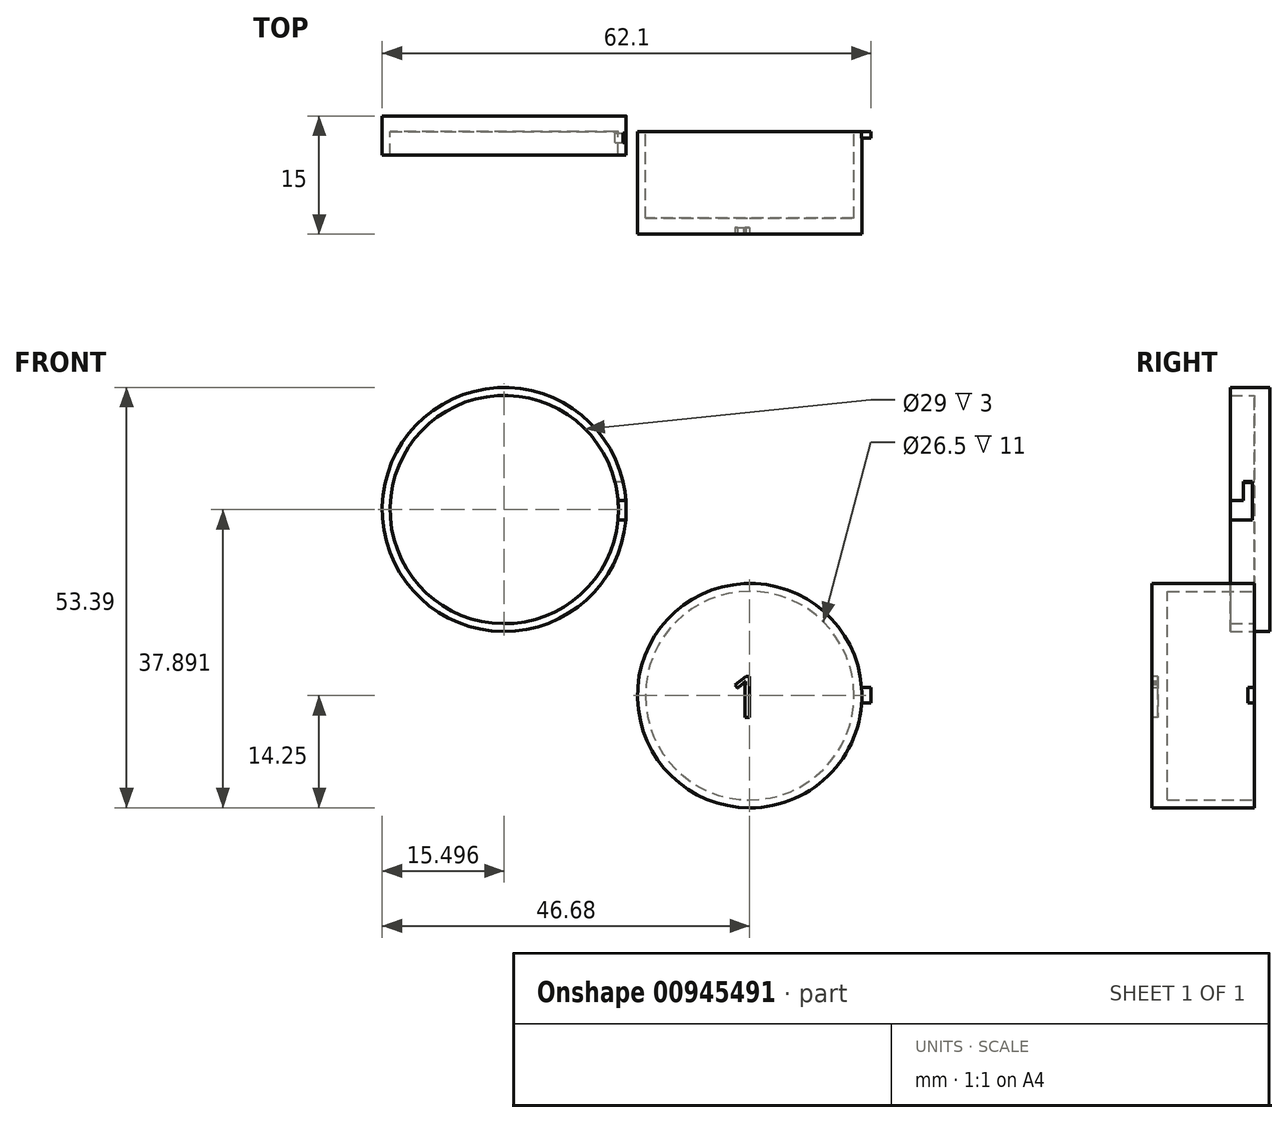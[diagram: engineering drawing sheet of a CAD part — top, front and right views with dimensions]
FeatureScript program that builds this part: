
annotation { "Feature Type Name" : "Feature", "Feature Type Description" : "" }
export const myFeature = defineFeature(function(context is Context, id is Id, definition is map)
    precondition{}
    {
        {
            var Q0;
            Q0=qCreatedBy(makeId("Front.planeOp"),FACE);
            var sketch = newSketch(context, id + "F0", { "sketchPlane" : qUnion([Q0])});
            skCircle(sketch, "E0", {"center": v(0, 0) * mm, "radius": 13.25 * mm});
            skCircle(sketch, "E1", {"center": v(0, 0) * mm, "radius": 14.25 * mm});
            skSolve(sketch);
        }
        {
            var Q0;
            Q0=makeQuery(id+"F0.imprint","IMPRINT",FACE,{"disambiguationData":[TD([[makeQuery(id+"F0.imprint","IMPRINT",EDGE,{"derivedFrom":sQuery(id+"F0.wireOp",EDGE,"E0")}),-1.0]])]});
            extrude(context, id + "F1", {"entities" : qUnion([Q0]), "depth" : 11 * mm, "offsetDistance" : 25 * mm});
        }
        {
            var Q0;
            Q0=makeQuery(id+"F1.opExtrude","CAP_FACE",FACE,{"disambiguationData":[OSD([sQuery(id+"F0.wireOp",EDGE,"E0"),sQuery(id+"F0.wireOp",EDGE,"E1")])],"isStart":false});
            var sketch = newSketch(context, id + "F2", { "sketchPlane" : qUnion([Q0])});
            skCircle(sketch, "E2", {"center": v(0, 0) * mm, "radius": 14.25 * mm});
            skSolve(sketch);
        }
        {
            var Q0;
            Q0 = qSketchRegion(id + "F2", true);
            extrude(context, id + "F3", {"entities" : qUnion([Q0]), "operationType" : NewBodyOperationType.ADD, "depth" : 2 * mm, "offsetDistance" : 25 * mm});
        }
        {
            var Q0;
            Q0=qCreatedBy(makeId("Front.planeOp"),FACE);
            var sketch = newSketch(context, id + "F4", { "sketchPlane" : qUnion([Q0])});
            skCircle(sketch, "E3", {"center": v(-31.18, 23.64) * mm, "radius": 14.5 * mm});
            skCircle(sketch, "E4", {"center": v(-31.18, 23.64) * mm, "radius": 15.5 * mm});
            skSolve(sketch);
        }
        {
            var Q0;
            Q0=makeQuery(id+"F4.imprint","IMPRINT",FACE,{"disambiguationData":[TD([[makeQuery(id+"F4.imprint","IMPRINT",EDGE,{"derivedFrom":sQuery(id+"F4.wireOp",EDGE,"E3")}),-1.0]])]});
            extrude(context, id + "F5", {"entities" : qUnion([Q0]), "depth" : 3 * mm, "offsetDistance" : 25 * mm});
        }
        {
            var Q0;
            Q0=makeQuery(id+"F5.opExtrude","CAP_FACE",FACE,{"disambiguationData":[OSD([sQuery(id+"F4.wireOp",EDGE,"E3"),sQuery(id+"F4.wireOp",EDGE,"E4")])],"isStart":true});
            var sketch = newSketch(context, id + "F6", { "sketchPlane" : qUnion([Q0])});
            skCircle(sketch, "E5", {"center": v(31.18, 23.64) * mm, "radius": 15.5 * mm});
            skSolve(sketch);
        }
        {
            var Q0;
            Q0 = qSketchRegion(id + "F6", true);
            extrude(context, id + "F7", {"entities" : qUnion([Q0]), "operationType" : NewBodyOperationType.ADD, "depth" : 2 * mm, "offsetDistance" : 25 * mm});
        }
        {
            var Q0;
            Q0=makeQuery(id+"F1.opExtrude","CAP_FACE",FACE,{"disambiguationData":[OSD([sQuery(id+"F0.wireOp",EDGE,"E0"),sQuery(id+"F0.wireOp",EDGE,"E1")])],"isStart":true});
            var sketch = newSketch(context, id + "F8", { "sketchPlane" : qUnion([Q0])});
            skLineSegment(sketch, "E6.bottom", {"start": v(-14.22, -0.95) * mm, "end": v(-15.42, -0.95) * mm});
            skLineSegment(sketch, "E6.top", {"start": v(-14.22, 1.05) * mm, "end": v(-15.42, 1.05) * mm});
            skLineSegment(sketch, "E6.left", {"start": v(-14.22, -0.95) * mm, "end": v(-14.22, 1.05) * mm});
            skLineSegment(sketch, "E6.right", {"start": v(-15.42, -0.95) * mm, "end": v(-15.42, 1.05) * mm});
            skSolve(sketch);
        }
        {
            var Q0;
            {var subQ4=sQuery(id+"F8.wireOp",EDGE,"E6.bottom");Q0=makeQuery(id+"F8.imprint","IMPRINT",FACE,{"disambiguationData":[TD([[makeQuery(id+"F8.imprint","IMPRINT",EDGE,{"derivedFrom":subQ4}),-1.0]])]});}
            extrude(context, id + "F9", {"entities" : qUnion([Q0]), "operationType" : NewBodyOperationType.ADD, "oppositeDirection" : true, "depth" : 0.8 * mm, "offsetDistance" : 25 * mm});
        }
        {
            var Q0;
            Q0=makeQuery(id+"F5.opExtrude","CAP_FACE",FACE,{"disambiguationData":[OSD([sQuery(id+"F4.wireOp",EDGE,"E3"),sQuery(id+"F4.wireOp",EDGE,"E4")])],"isStart":false});
            var sketch = newSketch(context, id + "F10", { "sketchPlane" : qUnion([Q0])});
            skLineSegment(sketch, "E7.bottom", {"start": v(-17.06, 22.3) * mm, "end": v(-15.06, 22.3) * mm});
            skLineSegment(sketch, "E7.right", {"start": v(-15.06, 22.3) * mm, "end": v(-15.06, 24.8) * mm});
            skLineSegment(sketch, "E8", {"start": v(-15.06, 24.8) * mm, "end": v(-17.06, 24.8) * mm});
            skLineSegment(sketch, "E9", {"start": v(-17.06, 24.8) * mm, "end": v(-17.06, 22.3) * mm});
            skSolve(sketch);
        }
        {
            var Q0;
            Q0 = qSketchRegion(id + "F10", true);
            extrude(context, id + "F11", {"entities" : qUnion([Q0]), "operationType" : NewBodyOperationType.REMOVE, "oppositeDirection" : true, "depth" : 2.8 * mm, "offsetDistance" : 25 * mm});
        }
        {
            var Q0;
            Q0=makeQuery(id+"F11.boolean.opBoolean","COPY",FACE,{"derivedFrom":makeQuery(id+"F11.opExtrude","SWEPT_FACE",FACE,{"disambiguationData":[OSD([sQuery(id+"F10.wireOp",EDGE,"E8")])]})});
            var sketch = newSketch(context, id + "F12", { "sketchPlane" : qUnion([Q0])});
            skLineSegment(sketch, "E10.left", {"start": v(-17.1, 0.2) * mm, "end": v(-17.1, 1.4) * mm});
            skLineSegment(sketch, "E10.right", {"start": v(-15.18, 0.2) * mm, "end": v(-15.18, 1.4) * mm});
            skLineSegment(sketch, "E11", {"start": v(-17.1, 1.4) * mm, "end": v(-15.18, 1.4) * mm});
            skLineSegment(sketch, "E12", {"start": v(-17.1, 0.2) * mm, "end": v(-15.18, 0.2) * mm});
            skSolve(sketch);
        }
        {
            var Q0;
            Q0 = qSketchRegion(id + "F12", true);
            extrude(context, id + "F13", {"entities" : qUnion([Q0]), "operationType" : NewBodyOperationType.REMOVE, "oppositeDirection" : true, "depth" : 2.4 * mm, "offsetDistance" : 25 * mm});
        }
        {
            var Q0;
            Q0=makeQuery(id+"F3.opExtrude","CAP_FACE",FACE,{"disambiguationData":[OSD([sQuery(id+"F2.wireOp",EDGE,"E2")])],"isStart":false});
            var sketch = newSketch(context, id + "F14", { "sketchPlane" : qUnion([Q0])});
            skText(sketch, "E13", { "text": "1", "fontName": "OpenSans-Regular.ttf"});
            const initialGuessF14  = {"E13": [-0.00254, -0.00277, 1, 0, 0.00524]};
            skSetInitialGuess(sketch, initialGuessF14);
            skSolve(sketch);
        }
        {
            var Q0;
            Q0 = qSketchRegion(id + "F14", true);
            extrude(context, id + "F15", {"entities" : qUnion([Q0]), "operationType" : NewBodyOperationType.REMOVE, "oppositeDirection" : true, "depth" : 0.8 * mm, "offsetDistance" : 25 * mm});
        }
    });
